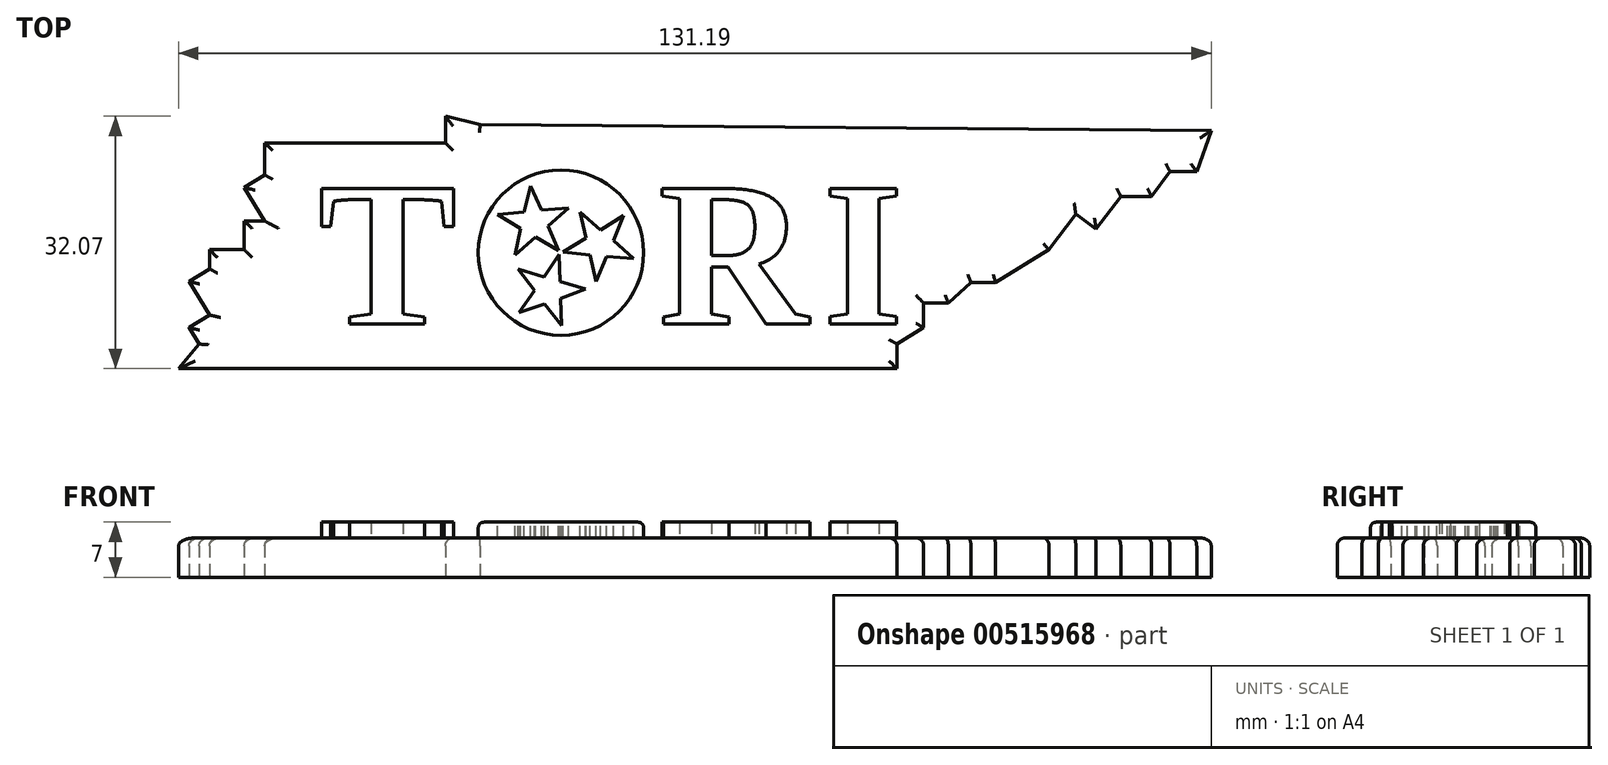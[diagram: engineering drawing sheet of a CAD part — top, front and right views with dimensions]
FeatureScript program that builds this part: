
annotation { "Feature Type Name" : "Feature", "Feature Type Description" : "" }
export const myFeature = defineFeature(function(context is Context, id is Id, definition is map)
    precondition{}
    {
        {
            var Q0;
            Q0=qCreatedBy(makeId("Top.planeOp"),FACE);
            var sketch = newSketch(context, id + "F0", { "sketchPlane" : qUnion([Q0])});
            skLineSegment(sketch, "E0", {"start": v(64.67, 9.9) * mm, "end": v(61.28, 9.9) * mm});
            skLineSegment(sketch, "E1", {"start": v(61.28, 9.9) * mm, "end": v(58.93, 6.78) * mm});
            skLineSegment(sketch, "E2", {"start": v(58.93, 6.78) * mm, "end": v(55.02, 6.78) * mm});
            skLineSegment(sketch, "E3", {"start": v(55.02, 6.78) * mm, "end": v(51.9, 2.6) * mm});
            skLineSegment(sketch, "E4", {"start": v(51.9, 2.6) * mm, "end": v(49.3, 4.55) * mm});
            skLineSegment(sketch, "E5", {"start": v(49.3, 4.55) * mm, "end": v(45.9, 0) * mm});
            skLineSegment(sketch, "E6", {"start": v(45.9, 0) * mm, "end": v(42.5, -2.09) * mm});
            skLineSegment(sketch, "E7", {"start": v(42.5, -2.09) * mm, "end": v(39.11, -4.17) * mm});
            skLineSegment(sketch, "E8", {"start": v(39.11, -4.17) * mm, "end": v(35.99, -4.17) * mm});
            skLineSegment(sketch, "E9", {"start": v(35.99, -4.17) * mm, "end": v(33.12, -6.78) * mm});
            skLineSegment(sketch, "E10", {"start": v(33.12, -6.78) * mm, "end": v(29.99, -6.78) * mm});
            skLineSegment(sketch, "E11", {"start": v(29.99, -6.78) * mm, "end": v(29.99, -9.9) * mm});
            skLineSegment(sketch, "E12", {"start": v(29.99, -9.9) * mm, "end": v(26.6, -12) * mm});
            skLineSegment(sketch, "E13", {"start": v(26.6, -12) * mm, "end": v(26.6, -15.12) * mm});
            skLineSegment(sketch, "E14", {"start": v(26.6, -15.12) * mm, "end": v(-64.67, -15.12) * mm});
            skLineSegment(sketch, "E15", {"start": v(-64.67, -15.12) * mm, "end": v(-62.06, -12) * mm});
            skLineSegment(sketch, "E16", {"start": v(-62.06, -12) * mm, "end": v(-63.35, -9.9) * mm});
            skLineSegment(sketch, "E17", {"start": v(-63.35, -9.9) * mm, "end": v(-60.73, -8.3) * mm});
            skLineSegment(sketch, "E18", {"start": v(-60.73, -8.3) * mm, "end": v(-63.35, -4.04) * mm});
            skLineSegment(sketch, "E19", {"start": v(-63.35, -4.04) * mm, "end": v(-60.73, -2.43) * mm});
            skLineSegment(sketch, "E20", {"start": v(-60.73, -2.43) * mm, "end": v(-60.73, 0) * mm});
            skLineSegment(sketch, "E21", {"start": v(-60.73, 0) * mm, "end": v(-56.32, 0) * mm});
            skLineSegment(sketch, "E22", {"start": v(-56.32, 0) * mm, "end": v(-56.32, 3.65) * mm});
            skLineSegment(sketch, "E23", {"start": v(-56.32, 3.65) * mm, "end": v(-53.72, 3.65) * mm});
            skLineSegment(sketch, "E24", {"start": v(-53.72, 3.65) * mm, "end": v(-55.02, 5.77) * mm});
            skLineSegment(sketch, "E25", {"start": v(-55.02, 5.77) * mm, "end": v(-56.32, 7.89) * mm});
            skLineSegment(sketch, "E26", {"start": v(-56.32, 7.89) * mm, "end": v(-53.72, 9.5) * mm});
            skLineSegment(sketch, "E27", {"start": v(-53.72, 9.5) * mm, "end": v(-53.72, 13.56) * mm});
            skLineSegment(sketch, "E28", {"start": v(-53.72, 13.56) * mm, "end": v(-30.77, 13.56) * mm});
            skLineSegment(sketch, "E29", {"start": v(-30.77, 13.56) * mm, "end": v(-30.77, 16.95) * mm});
            skLineSegment(sketch, "E30", {"start": v(-30.77, 16.95) * mm, "end": v(-26.34, 15.9) * mm});
            skLineSegment(sketch, "E31", {"start": v(64.67, 9.9) * mm, "end": v(66.52, 15.14) * mm});
            skLineSegment(sketch, "E32", {"start": v(66.52, 15.14) * mm, "end": v(-26.34, 15.9) * mm});
            skSolve(sketch);
        }
        {
            var Q0;
            Q0=makeQuery(id+"F0.imprint","IMPRINT",FACE,{"disambiguationData":[TD([[makeQuery(id+"F0.imprint","IMPRINT",EDGE,{"derivedFrom":sQuery(id+"F0.wireOp",EDGE,"E0")}),-1.0]])]});
            extrude(context, id + "F1", {"entities" : qUnion([Q0]), "depth" : 5 * mm, "offsetDistance" : 25 * mm});
        }
        {
            var Q0;
            Q0=makeQuery(id+"F1.opExtrude","CAP_FACE",FACE,{"disambiguationData":[OSD([sQuery(id+"F0.wireOp",EDGE,"E0"),sQuery(id+"F0.wireOp",EDGE,"E1"),sQuery(id+"F0.wireOp",EDGE,"E2"),sQuery(id+"F0.wireOp",EDGE,"E3"),sQuery(id+"F0.wireOp",EDGE,"E4"),sQuery(id+"F0.wireOp",EDGE,"E5"),sQuery(id+"F0.wireOp",EDGE,"E6"),sQuery(id+"F0.wireOp",EDGE,"E7"),sQuery(id+"F0.wireOp",EDGE,"E8"),sQuery(id+"F0.wireOp",EDGE,"E9"),sQuery(id+"F0.wireOp",EDGE,"E10"),sQuery(id+"F0.wireOp",EDGE,"E11"),sQuery(id+"F0.wireOp",EDGE,"E12"),sQuery(id+"F0.wireOp",EDGE,"E13"),sQuery(id+"F0.wireOp",EDGE,"E14"),sQuery(id+"F0.wireOp",EDGE,"E15"),sQuery(id+"F0.wireOp",EDGE,"E16"),sQuery(id+"F0.wireOp",EDGE,"E17"),sQuery(id+"F0.wireOp",EDGE,"E18"),sQuery(id+"F0.wireOp",EDGE,"E19"),sQuery(id+"F0.wireOp",EDGE,"E20"),sQuery(id+"F0.wireOp",EDGE,"E21"),sQuery(id+"F0.wireOp",EDGE,"E22"),sQuery(id+"F0.wireOp",EDGE,"E23"),sQuery(id+"F0.wireOp",EDGE,"E24"),sQuery(id+"F0.wireOp",EDGE,"E25"),sQuery(id+"F0.wireOp",EDGE,"E26"),sQuery(id+"F0.wireOp",EDGE,"E27"),sQuery(id+"F0.wireOp",EDGE,"E28"),sQuery(id+"F0.wireOp",EDGE,"E29"),sQuery(id+"F0.wireOp",EDGE,"E30"),sQuery(id+"F0.wireOp",EDGE,"E31"),sQuery(id+"F0.wireOp",EDGE,"E32")])],"isStart":false});
            var sketch = newSketch(context, id + "F2", { "sketchPlane" : qUnion([Q0])});
            skPoint(sketch, "E33.firstSnap0", {"position": v(-28.55, 16.43) * mm});
            skText(sketch, "E34", { "text": "T", "fontName": "Tinos-Bold.ttf"});
            skCircle(sketch, "E35", {"center": v(-16.08, -0.39) * mm, "radius": 10.5 * mm});
            skPoint(sketch, "E35.centerSnap0", {"position": v(-28.1, 0) * mm});
            skText(sketch, "E36", { "text": "R", "fontName": "Tinos-Bold.ttf"});
            skText(sketch, "E37", { "text": "I", "fontName": "Tinos-Bold.ttf"});
            const initialGuessF2  = {"E34": [-0.0469, -0.00947, 1, 0, 0.01894], "E36": [-0.00369, -0.00947, 1, 0, 0.01894], "E37": [0.01719, -0.00947, 1, 0, 0.01894]};
            skSetInitialGuess(sketch, initialGuessF2);
            skSolve(sketch);
        }
        {
            var Q0;
            Q0=makeQuery(id+"F2.imprint","IMPRINT",FACE,{"disambiguationData":[TD([[makeQuery(id+"F2.imprint","IMPRINT",EDGE,{"derivedFrom":sQuery(id+"F2.wireOp",EDGE,"E34.sketch_text.stroke-0")}),-1.0]])]});
            var Q1;
            Q1=makeQuery(id+"F2.imprint","IMPRINT",FACE,{"disambiguationData":[TD([[makeQuery(id+"F2.imprint","IMPRINT",EDGE,{"derivedFrom":sQuery(id+"F2.wireOp",EDGE,"E35")}),1.0]])]});
            var Q2;
            Q2=makeQuery(id+"F2.imprint","IMPRINT",FACE,{"disambiguationData":[TD([[makeQuery(id+"F2.imprint","IMPRINT",EDGE,{"derivedFrom":sQuery(id+"F2.wireOp",EDGE,"E36.sketch_text.stroke-0")}),-1.0]])]});
            var Q3;
            Q3=makeQuery(id+"F2.imprint","IMPRINT",FACE,{"disambiguationData":[TD([[makeQuery(id+"F2.imprint","IMPRINT",EDGE,{"derivedFrom":sQuery(id+"F2.wireOp",EDGE,"E37.sketch_text.stroke-0")}),-1.0]])]});
            extrude(context, id + "F3", {"entities" : qUnion([Q0, Q1, Q2, Q3]), "operationType" : NewBodyOperationType.ADD, "depth" : 2 * mm, "offsetDistance" : 25 * mm});
        }
        {
            var Q0;
            Q0=makeQuery(id+"F3.opExtrude","CAP_FACE",FACE,{"disambiguationData":[OSD([sQuery(id+"F2.wireOp",EDGE,"E35")])],"isStart":false});
            var sketch = newSketch(context, id + "F4", { "sketchPlane" : qUnion([Q0])});
            skLineSegment(sketch, "E38", {"start": v(-20.76, 4.8) * mm, "end": v(-19.96, 8.08) * mm});
            skLineSegment(sketch, "E39", {"start": v(-19.96, 8.08) * mm, "end": v(-18.57, 5.02) * mm});
            skLineSegment(sketch, "E40", {"start": v(-18.57, 5.02) * mm, "end": v(-15.16, 5.28) * mm});
            skLineSegment(sketch, "E41", {"start": v(-15.16, 5.28) * mm, "end": v(-17.7, 2.99) * mm});
            skLineSegment(sketch, "E42", {"start": v(-17.7, 2.99) * mm, "end": v(-16.4, -0.14) * mm});
            skLineSegment(sketch, "E43", {"start": v(-16.4, -0.14) * mm, "end": v(-19.3, 1.6) * mm});
            skLineSegment(sketch, "E44", {"start": v(-19.3, 1.6) * mm, "end": v(-21.95, -0.67) * mm});
            skLineSegment(sketch, "E45", {"start": v(-21.95, -0.67) * mm, "end": v(-21.21, 2.66) * mm});
            skLineSegment(sketch, "E46", {"start": v(-21.21, 2.66) * mm, "end": v(-24.14, 4.45) * mm});
            skLineSegment(sketch, "E47", {"start": v(-24.14, 4.45) * mm, "end": v(-20.76, 4.8) * mm});
            skLineSegment(sketch, "E48", {"start": v(-15.82, -0.3) * mm, "end": v(-12.89, 1.47) * mm});
            skLineSegment(sketch, "E49", {"start": v(-12.89, 1.47) * mm, "end": v(-13.66, 4.8) * mm});
            skLineSegment(sketch, "E50", {"start": v(-13.66, 4.8) * mm, "end": v(-11.08, 2.52) * mm});
            skLineSegment(sketch, "E51", {"start": v(-11.08, 2.52) * mm, "end": v(-8.13, 4.32) * mm});
            skLineSegment(sketch, "E52", {"start": v(-8.13, 4.32) * mm, "end": v(-9.42, 1.17) * mm});
            skLineSegment(sketch, "E53", {"start": v(-9.42, 1.17) * mm, "end": v(-6.85, -1.11) * mm});
            skLineSegment(sketch, "E54", {"start": v(-6.85, -1.11) * mm, "end": v(-10.28, -0.84) * mm});
            skLineSegment(sketch, "E55", {"start": v(-10.28, -0.84) * mm, "end": v(-11.6, -4.02) * mm});
            skLineSegment(sketch, "E56", {"start": v(-11.6, -4.02) * mm, "end": v(-12.4, -0.66) * mm});
            skLineSegment(sketch, "E57", {"start": v(-12.4, -0.66) * mm, "end": v(-15.82, -0.3) * mm});
            skLineSegment(sketch, "E58", {"start": v(-21.44, -8) * mm, "end": v(-19.47, -5.2) * mm});
            skLineSegment(sketch, "E59", {"start": v(-19.47, -5.2) * mm, "end": v(-21.53, -2.48) * mm});
            skLineSegment(sketch, "E60", {"start": v(-21.53, -2.48) * mm, "end": v(-18.24, -3.45) * mm});
            skLineSegment(sketch, "E61", {"start": v(-18.24, -3.45) * mm, "end": v(-16.33, -0.62) * mm});
            skLineSegment(sketch, "E62", {"start": v(-16.33, -0.62) * mm, "end": v(-16.2, -4.07) * mm});
            skLineSegment(sketch, "E63", {"start": v(-16.2, -4.07) * mm, "end": v(-12.93, -5.02) * mm});
            skLineSegment(sketch, "E64", {"start": v(-12.93, -5.02) * mm, "end": v(-16.15, -6.19) * mm});
            skLineSegment(sketch, "E65", {"start": v(-16.15, -6.19) * mm, "end": v(-16.03, -9.65) * mm});
            skLineSegment(sketch, "E66", {"start": v(-16.03, -9.65) * mm, "end": v(-18.15, -6.92) * mm});
            skLineSegment(sketch, "E67", {"start": v(-18.15, -6.92) * mm, "end": v(-21.44, -8) * mm});
            skSolve(sketch);
        }
        {
            var Q0;
            Q0=makeQuery(id+"F4.imprint","IMPRINT",FACE,{"disambiguationData":[TD([[makeQuery(id+"F4.imprint","IMPRINT",EDGE,{"derivedFrom":sQuery(id+"F4.wireOp",EDGE,"E38")}),-1.0]])]});
            var Q1;
            Q1=makeQuery(id+"F4.imprint","IMPRINT",FACE,{"disambiguationData":[TD([[makeQuery(id+"F4.imprint","IMPRINT",EDGE,{"derivedFrom":sQuery(id+"F4.wireOp",EDGE,"E58")}),-1.0]])]});
            var Q2;
            Q2=makeQuery(id+"F4.imprint","IMPRINT",FACE,{"disambiguationData":[TD([[makeQuery(id+"F4.imprint","IMPRINT",EDGE,{"derivedFrom":sQuery(id+"F4.wireOp",EDGE,"E48")}),-1.0]])]});
            extrude(context, id + "F5", {"entities" : qUnion([Q0, Q1, Q2]), "operationType" : NewBodyOperationType.REMOVE, "oppositeDirection" : true, "depth" : 2 * mm, "offsetDistance" : 25 * mm});
        }
        {
            var Q0;
            Q0=makeQuery(id+"F1.opExtrude","CAP_EDGE",EDGE,{"disambiguationData":[OSD([sQuery(id+"F0.wireOp",EDGE,"E30")])],"isStart":false});
            var Q1;
            Q1=makeQuery(id+"F1.opExtrude","CAP_EDGE",EDGE,{"disambiguationData":[OSD([sQuery(id+"F0.wireOp",EDGE,"E28")])],"isStart":false});
            var Q2;
            Q2=makeQuery(id+"F1.opExtrude","CAP_EDGE",EDGE,{"disambiguationData":[OSD([sQuery(id+"F0.wireOp",EDGE,"E27")])],"isStart":false});
            var Q3;
            Q3=makeQuery(id+"F1.opExtrude","CAP_EDGE",EDGE,{"disambiguationData":[OSD([sQuery(id+"F0.wireOp",EDGE,"E26")])],"isStart":false});
            var Q4;
            Q4=makeQuery(id+"F1.opExtrude","CAP_EDGE",EDGE,{"disambiguationData":[OSD([sQuery(id+"F0.wireOp",EDGE,"E24"),sQuery(id+"F0.wireOp",EDGE,"E25")])],"isStart":false});
            var Q5;
            Q5=makeQuery(id+"F1.opExtrude","CAP_EDGE",EDGE,{"disambiguationData":[OSD([sQuery(id+"F0.wireOp",EDGE,"E29")])],"isStart":false});
            var Q6;
            Q6=makeQuery(id+"F1.opExtrude","CAP_EDGE",EDGE,{"disambiguationData":[OSD([sQuery(id+"F0.wireOp",EDGE,"E32")])],"isStart":false});
            var Q7;
            Q7=makeQuery(id+"F1.opExtrude","CAP_EDGE",EDGE,{"disambiguationData":[OSD([sQuery(id+"F0.wireOp",EDGE,"E23")])],"isStart":false});
            var Q8;
            Q8=makeQuery(id+"F1.opExtrude","CAP_EDGE",EDGE,{"disambiguationData":[OSD([sQuery(id+"F0.wireOp",EDGE,"E22")])],"isStart":false});
            var Q9;
            Q9=makeQuery(id+"F1.opExtrude","CAP_EDGE",EDGE,{"disambiguationData":[OSD([sQuery(id+"F0.wireOp",EDGE,"E21")])],"isStart":false});
            var Q10;
            Q10=makeQuery(id+"F1.opExtrude","CAP_EDGE",EDGE,{"disambiguationData":[OSD([sQuery(id+"F0.wireOp",EDGE,"E20")])],"isStart":false});
            var Q11;
            Q11=makeQuery(id+"F1.opExtrude","CAP_EDGE",EDGE,{"disambiguationData":[OSD([sQuery(id+"F0.wireOp",EDGE,"E19")])],"isStart":false});
            var Q12;
            Q12=makeQuery(id+"F1.opExtrude","CAP_EDGE",EDGE,{"disambiguationData":[OSD([sQuery(id+"F0.wireOp",EDGE,"E18")])],"isStart":false});
            var Q13;
            Q13=makeQuery(id+"F1.opExtrude","CAP_EDGE",EDGE,{"disambiguationData":[OSD([sQuery(id+"F0.wireOp",EDGE,"E17")])],"isStart":false});
            var Q14;
            Q14=makeQuery(id+"F1.opExtrude","CAP_EDGE",EDGE,{"disambiguationData":[OSD([sQuery(id+"F0.wireOp",EDGE,"E16")])],"isStart":false});
            var Q15;
            Q15=makeQuery(id+"F1.opExtrude","CAP_EDGE",EDGE,{"disambiguationData":[OSD([sQuery(id+"F0.wireOp",EDGE,"E15")])],"isStart":false});
            var Q16;
            Q16=makeQuery(id+"F1.opExtrude","CAP_EDGE",EDGE,{"disambiguationData":[OSD([sQuery(id+"F0.wireOp",EDGE,"E14")])],"isStart":false});
            var Q17;
            Q17=makeQuery(id+"F1.opExtrude","CAP_EDGE",EDGE,{"disambiguationData":[OSD([sQuery(id+"F0.wireOp",EDGE,"E13")])],"isStart":false});
            var Q18;
            Q18=makeQuery(id+"F1.opExtrude","CAP_EDGE",EDGE,{"disambiguationData":[OSD([sQuery(id+"F0.wireOp",EDGE,"E12")])],"isStart":false});
            var Q19;
            Q19=makeQuery(id+"F1.opExtrude","CAP_EDGE",EDGE,{"disambiguationData":[OSD([sQuery(id+"F0.wireOp",EDGE,"E11")])],"isStart":false});
            var Q20;
            Q20=makeQuery(id+"F1.opExtrude","CAP_EDGE",EDGE,{"disambiguationData":[OSD([sQuery(id+"F0.wireOp",EDGE,"E10")])],"isStart":false});
            var Q21;
            Q21=makeQuery(id+"F1.opExtrude","CAP_EDGE",EDGE,{"disambiguationData":[OSD([sQuery(id+"F0.wireOp",EDGE,"E9")])],"isStart":false});
            var Q22;
            Q22=makeQuery(id+"F1.opExtrude","CAP_EDGE",EDGE,{"disambiguationData":[OSD([sQuery(id+"F0.wireOp",EDGE,"E8")])],"isStart":false});
            var Q23;
            Q23=makeQuery(id+"F1.opExtrude","CAP_EDGE",EDGE,{"disambiguationData":[OSD([sQuery(id+"F0.wireOp",EDGE,"E6"),sQuery(id+"F0.wireOp",EDGE,"E7")])],"isStart":false});
            var Q24;
            Q24=makeQuery(id+"F1.opExtrude","CAP_EDGE",EDGE,{"disambiguationData":[OSD([sQuery(id+"F0.wireOp",EDGE,"E5")])],"isStart":false});
            var Q25;
            Q25=makeQuery(id+"F1.opExtrude","CAP_EDGE",EDGE,{"disambiguationData":[OSD([sQuery(id+"F0.wireOp",EDGE,"E4")])],"isStart":false});
            var Q26;
            Q26=makeQuery(id+"F1.opExtrude","CAP_EDGE",EDGE,{"disambiguationData":[OSD([sQuery(id+"F0.wireOp",EDGE,"E3")])],"isStart":false});
            var Q27;
            Q27=makeQuery(id+"F1.opExtrude","CAP_EDGE",EDGE,{"disambiguationData":[OSD([sQuery(id+"F0.wireOp",EDGE,"E2")])],"isStart":false});
            var Q28;
            Q28=makeQuery(id+"F1.opExtrude","CAP_EDGE",EDGE,{"disambiguationData":[OSD([sQuery(id+"F0.wireOp",EDGE,"E1")])],"isStart":false});
            var Q29;
            Q29=makeQuery(id+"F1.opExtrude","CAP_EDGE",EDGE,{"disambiguationData":[OSD([sQuery(id+"F0.wireOp",EDGE,"E0")])],"isStart":false});
            var Q30;
            Q30=makeQuery(id+"F1.opExtrude","CAP_EDGE",EDGE,{"disambiguationData":[OSD([sQuery(id+"F0.wireOp",EDGE,"E31")])],"isStart":false});
            fillet(context, id + "F6", {"entities" : qUnion([Q0, Q1, Q2, Q3, Q4, Q5, Q6, Q7, Q8, Q9, Q10, Q11, Q12, Q13, Q14, Q15, Q16, Q17, Q18, Q19, Q20, Q21, Q22, Q23, Q24, Q25, Q26, Q27, Q28, Q29, Q30]), "radius" : 1 * mm, "tangentPropagation" : true, "allowEdgeOverflow" : false});
        }
        {
            var Q0;
            Q0=makeQuery(id+"F3.opExtrude","CAP_EDGE",EDGE,{"disambiguationData":[OSD([sQuery(id+"F2.wireOp",EDGE,"E35")])],"isStart":false});
            fillet(context, id + "F7", {"entities" : qUnion([Q0]), "radius" : .7 * mm, "tangentPropagation" : true, "allowEdgeOverflow" : false});
        }
    });
